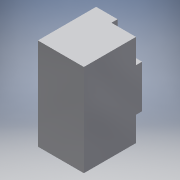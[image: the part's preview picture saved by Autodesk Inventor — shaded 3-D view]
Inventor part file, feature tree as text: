
AUTODESK INVENTOR PART (.ipt)
format: ipt  version: 2018 (Build 220112000, 112)  size: 140,800 bytes
history: native  units: mm
features: extrude x3, sketch x3, projected_geometry x3
ambient origin geometry x8: Origin, YZ Plane, XZ Plane, XY Plane, X Axis, Y Axis, Z Axis, Center Point
bodies: Volumenkörper1 (feature_tree)
feature tree (9):
  extrude  "Extrusion1"  Depth=150.0mm
  extrude  "Extrusion2"  Depth=80.0mm
  extrude  "Extrusion3"  Depth=80.0mm
  sketch  "Skizze1"  dims[d0=300.0mm d1=150.0mm]
  sketch  "Skizze2"  dims[d2=190.0mm d3=0.0mm d4=80.0mm]
  projected_geometry  "Projizierte Kontur1"
  sketch  "Skizze3"  dims[d5=80.0mm d6=80.0mm d7=80.0mm d8=20.0mm d9=20.0mm d10=20.0mm d11=0.0mm d12=15.0mm d13=15.0mm d14=20.0mm d15=0.0mm d16=40.0mm d17=40.0mm d18=40.0mm d19=40.0mm]
  projected_geometry  "Projizierte Kontur2"
  projected_geometry  "Projizierte Kontur3"
